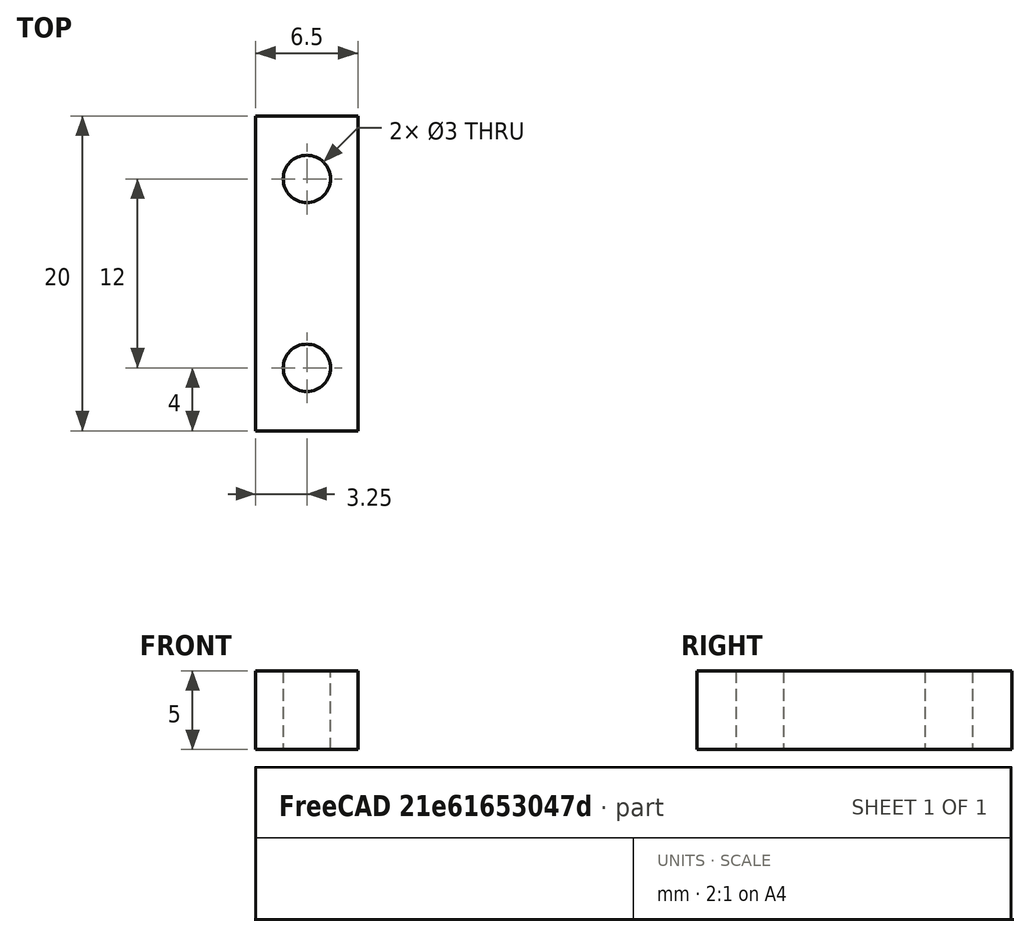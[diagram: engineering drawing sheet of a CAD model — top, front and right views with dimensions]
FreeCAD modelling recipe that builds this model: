
FCSTD DOCUMENT  (FreeCAD 0.16R6707 (Git))
Label: blocage_barres_verticales_haut
License: All rights reserved
LicenseURL: http://en.wikipedia.org/wiki/All_rights_reserved
objects: Sketcher::SketchObject×1, PartDesign::Pad×1
note: 3 computed .brp shape members not serialized (recipe doc carries the construction recipe); baked Part::Feature solids carry a one-line shape summary decoded from their .brp

FEATURE [Sketcher::SketchObject] Sketch
  sketch-geometry (7):
    g0: LineSegment StartX=0 StartY=0 StartZ=0 EndX=6.5 EndY=0 EndZ=0
    g1: LineSegment StartX=6.5 StartY=0 StartZ=0 EndX=6.5 EndY=20 EndZ=0
    g2: LineSegment StartX=6.5 StartY=20 StartZ=0 EndX=0 EndY=20 EndZ=0
    g3: LineSegment StartX=0 StartY=20 StartZ=0 EndX=0 EndY=0 EndZ=0
    g4: GeomPoint [constr] X=1.5 Y=10 Z=0
    g5: Circle CenterX=3.25 CenterY=16 CenterZ=0 NormalX=0 NormalY=0 NormalZ=1 Radius=1.5
    g6: Circle CenterX=3.25 CenterY=4 CenterZ=0 NormalX=0 NormalY=0 NormalZ=1 Radius=1.5
  constraints (19):
    c: Coincident(g0,g1)
    c: Coincident(g1,g2)
    c: Coincident(g2,g3)
    c: Coincident(g3,g0)
    c: Horizontal(g0)
    c: Horizontal(g2)
    c: Vertical(g1)
    c: Vertical(g3)
    c: Coincident(g0,g-1)
    c: Distance(g3) = 20
    c: Distance(g2) = 6.5
    c: DistanceY(g4) = 10
    c: DistanceX(g4) = 1.5
    c: Radius(g6) = 1.5
    c: Equal(g6,g5)
    c: DistanceX(g2,g5) = 3.25
    c: DistanceY(g5,g2) = 4
    c: DistanceY(g6) = 4
    c: DistanceX(g-1,g6) = 3.25
FEATURE [PartDesign::Pad] Pad
  Length = 5
  Length2 = 100
  Sketch = -> Sketch
  Type = 0
